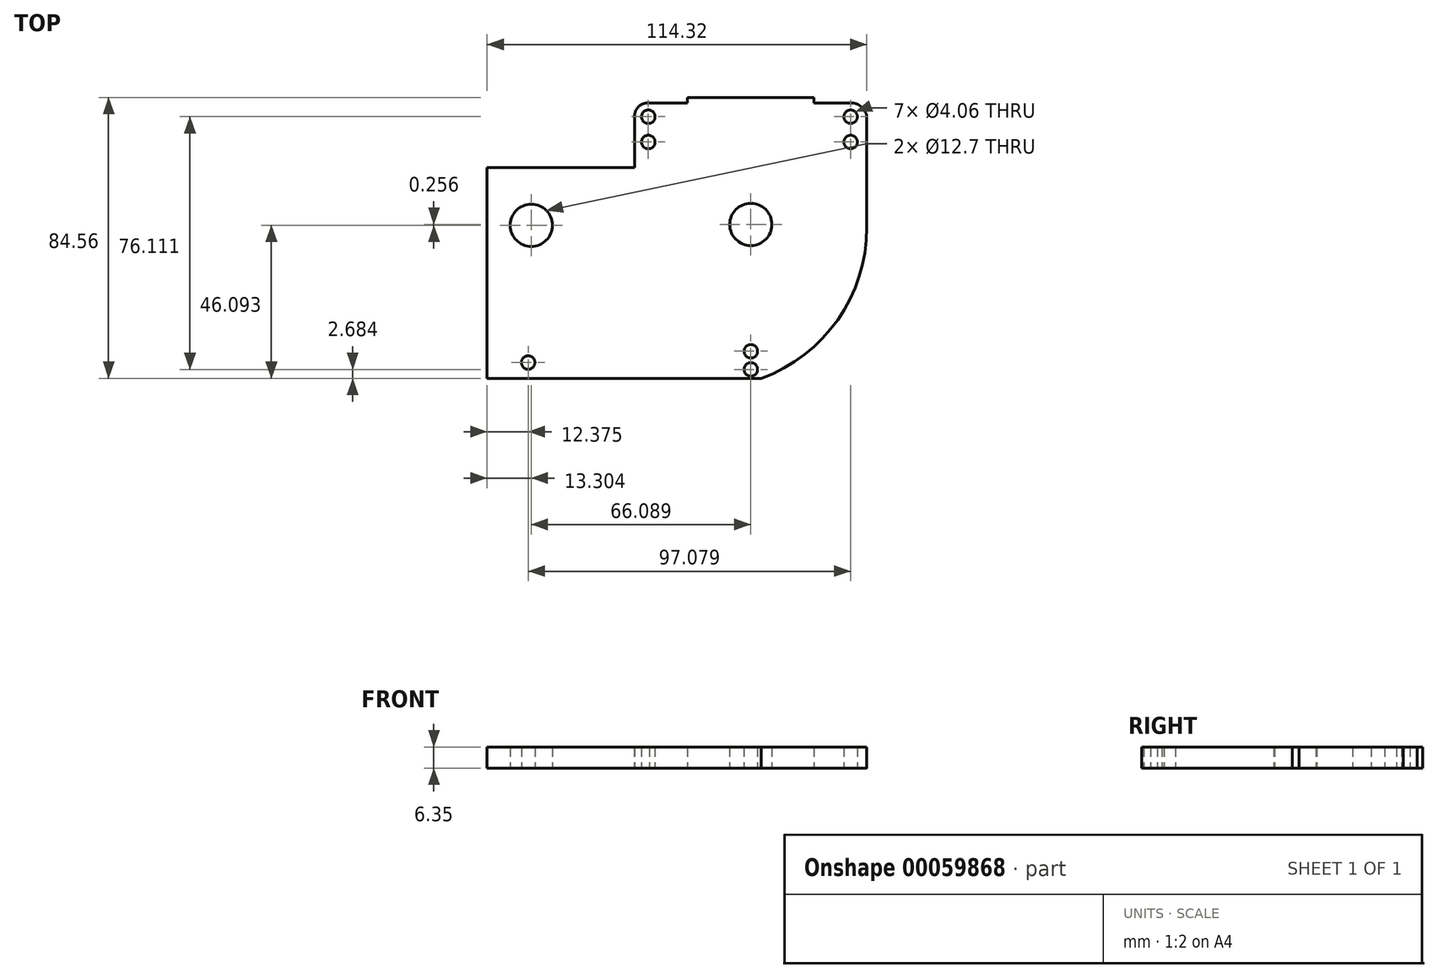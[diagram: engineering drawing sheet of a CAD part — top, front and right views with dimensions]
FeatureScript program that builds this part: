
annotation { "Feature Type Name" : "Feature", "Feature Type Description" : "" }
export const myFeature = defineFeature(function(context is Context, id is Id, definition is map)
    precondition{}
    {
        {
            var Q0;
            Q0=qCreatedBy(makeId("Top.planeOp"),FACE);
            var sketch = newSketch(context, id + "F0", { "sketchPlane" : qUnion([Q0])});
            skPoint(sketch, "E0.orphan", {"position": v(-132.19, 34.92) * mm});
            skPoint(sketch, "E1.start.orphan", {"position": v(-201.17, 34.92) * mm});
            skArc(sketch, "E2", {"start": v(-163.93, -49.64) * mm, "mid": v(-140.9, -31.96) * mm, "end": v(-132.19, -4.28) * mm});
            skPoint(sketch, "E3.start.orphan", {"position": v(-202.11, -2.52) * mm});
            skLineSegment(sketch, "E4", {"start": v(-132.19, -2.3) * mm, "end": v(-132.19, 29.16) * mm});
            skLineSegment(sketch, "E5", {"start": v(-202.11, 13.87) * mm, "end": v(-202.11, 29.16) * mm});
            skLineSegment(sketch, "E6", {"start": v(-186.15, 34.92) * mm, "end": v(-148.05, 34.92) * mm});
            skArc(sketch, "E7", {"start": v(-132.19, -4.28) * mm, "mid": v(-132.17, -3.3) * mm, "end": v(-132.19, -2.3) * mm});
            skLineSegment(sketch, "E8", {"start": v(-170.27, -49.64) * mm, "end": v(-240.8, -49.64) * mm});
            skPoint(sketch, "E9.start.orphan", {"position": v(-197.97, 34.92) * mm});
            skPoint(sketch, "E10.end.orphan", {"position": v(-137.04, 34) * mm});
            skPoint(sketch, "E11.endSnap0", {"position": v(-197.97, 28.06) * mm});
            skCircle(sketch, "E12", {"center": v(-234.11, -44.87) * mm, "radius": 2.03 * mm});
            skLineSegment(sketch, "E13", {"start": v(-198.24, 33.33) * mm, "end": v(-186.15, 33.33) * mm});
            skLineSegment(sketch, "E14", {"start": v(-186.15, 33.33) * mm, "end": v(-186.15, 34.92) * mm});
            skLineSegment(sketch, "E15", {"start": v(-148.05, 34.92) * mm, "end": v(-148.05, 33.33) * mm});
            skLineSegment(sketch, "E16", {"start": v(-132.19, -4.28) * mm, "end": v(-132.19, -2.3) * mm});
            skCircle(sketch, "E17", {"center": v(-197.97, 21.54) * mm, "radius": 2.03 * mm});
            skArc(sketch, "E18", {"start": v(-132.19, 29.16) * mm, "mid": v(-133.84, 32.14) * mm, "end": v(-137.04, 33.33) * mm});
            skArc(sketch, "E19", {"start": v(-197.7, 33.33) * mm, "mid": v(-201.02, 32.01) * mm, "end": v(-202.11, 28.6) * mm});
            skCircle(sketch, "E20", {"center": v(-167.1, -46.96) * mm, "radius": 2.03 * mm});
            skCircle(sketch, "E21", {"center": v(-137.04, 21.54) * mm, "radius": 2.03 * mm});
            skLineSegment(sketch, "E22.top", {"start": v(-170.27, -49.64) * mm, "end": v(-163.93, -49.64) * mm});
            skCircle(sketch, "E23", {"center": v(-167.1, -41.47) * mm, "radius": 2.03 * mm});
            skCircle(sketch, "E24", {"center": v(-137.04, 29.16) * mm, "radius": 2.03 * mm});
            skCircle(sketch, "E25", {"center": v(-197.97, 29.16) * mm, "radius": 2.03 * mm});
            skCircle(sketch, "E26", {"center": v(-233.19, -3.55) * mm, "radius": 6.35 * mm});
            skCircle(sketch, "E27", {"center": v(-167.1, -3.3) * mm, "radius": 6.35 * mm});
            skLineSegment(sketch, "E28", {"start": v(-240.8, -49.64) * mm, "end": v(-163.93, -49.64) * mm});
            skLineSegment(sketch, "E29", {"start": v(-148.05, 33.33) * mm, "end": v(-137.04, 33.33) * mm});
            skPoint(sketch, "E30.endSnap0", {"position": v(-242.08, -3.42) * mm});
            skLineSegment(sketch, "E31", {"start": v(-202.11, 13.87) * mm, "end": v(-246.49, 13.87) * mm});
            skLineSegment(sketch, "E32", {"start": v(-246.49, 13.87) * mm, "end": v(-246.49, -49.64) * mm});
            skLineSegment(sketch, "E33", {"start": v(-246.49, -49.64) * mm, "end": v(-240.8, -49.64) * mm});
            skSolve(sketch);
        }
        {
            var Q0;
            Q0 = qSketchRegion(id + "F0", true);
            extrude(context, id + "F1", {"entities" : qUnion([Q0]), "depth" : 6.35 * mm});
        }
    });
